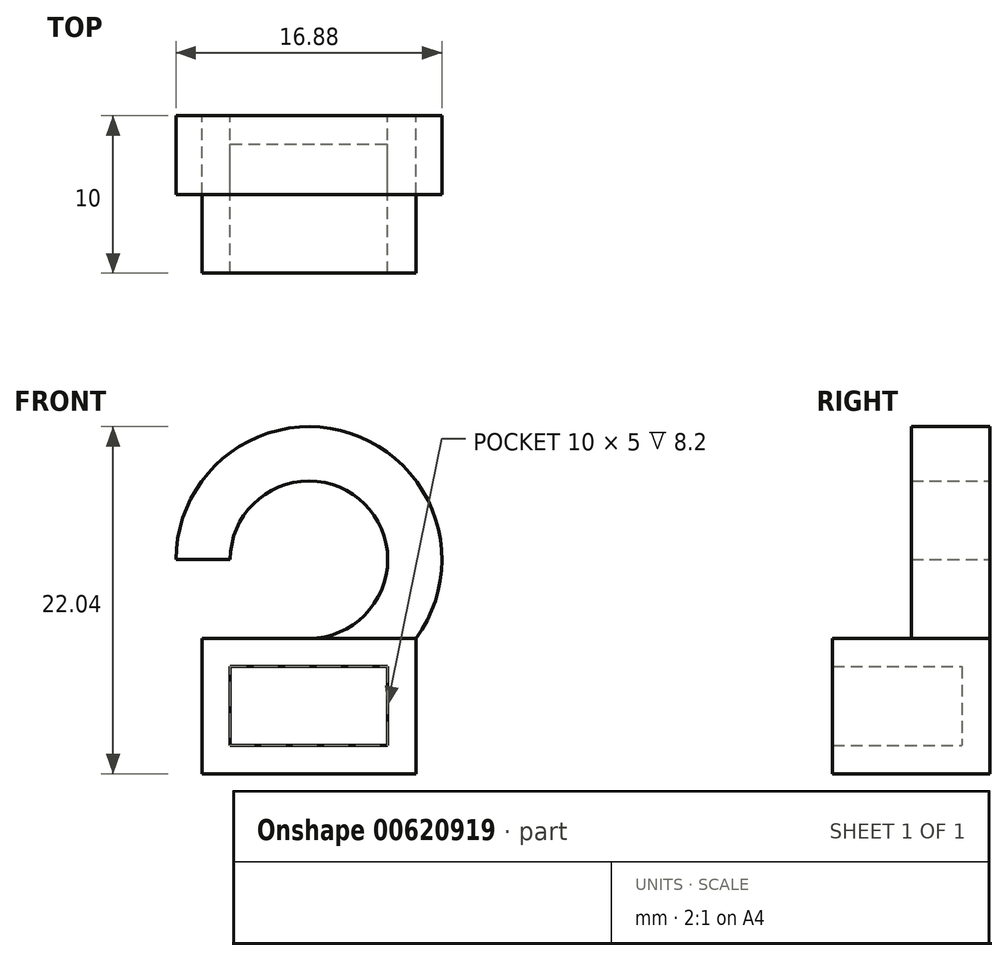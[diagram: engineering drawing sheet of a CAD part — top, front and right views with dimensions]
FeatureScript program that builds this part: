
annotation { "Feature Type Name" : "Feature", "Feature Type Description" : "" }
export const myFeature = defineFeature(function(context is Context, id is Id, definition is map)
    precondition{}
    {
        {
            var Q0;
            Q0=qCreatedBy(makeId("Front.planeOp"),FACE);
            var sketch = newSketch(context, id + "F0", { "sketchPlane" : qUnion([Q0])});
            skLineSegment(sketch, "E0.bottom", {"start": v(-5, 2.5) * mm, "end": v(5, 2.5) * mm});
            skLineSegment(sketch, "E0.top", {"start": v(-5, -2.5) * mm, "end": v(5, -2.5) * mm});
            skLineSegment(sketch, "E0.left", {"start": v(-5, 2.5) * mm, "end": v(-5, -2.5) * mm});
            skLineSegment(sketch, "E0.right", {"start": v(5, 2.5) * mm, "end": v(5, -2.5) * mm});
            skPoint(sketch, "E0.middle", {"position": v(0, 0) * mm});
            skLineSegment(sketch, "E1.bottom", {"start": v(-6.8, 4.3) * mm, "end": v(6.8, 4.3) * mm});
            skLineSegment(sketch, "E1.top", {"start": v(-6.8, -4.3) * mm, "end": v(6.8, -4.3) * mm});
            skLineSegment(sketch, "E1.left", {"start": v(-6.8, 4.3) * mm, "end": v(-6.8, -4.3) * mm});
            skLineSegment(sketch, "E1.right", {"start": v(6.8, 4.3) * mm, "end": v(6.8, -4.3) * mm});
            skLineSegment(sketch, "E2", {"start": v(0, 4.3) * mm, "end": v(0, 9.3) * mm});
            skPoint(sketch, "E2.endSnap0", {"position": v(0, 4.3) * mm});
            skArc(sketch, "E3", {"start": v(0, 4.3) * mm, "mid": v(3.54, 12.84) * mm, "end": v(-5, 9.3) * mm});
            skArc(sketch, "E4", {"start": v(-6.8, 4.3) * mm, "mid": v(8.02, 11.93) * mm, "end": v(-8.44, 9.3) * mm});
            skLineSegment(sketch, "E5", {"start": v(0, 9.3) * mm, "end": v(-8.44, 9.3) * mm});
            skSolve(sketch);
        }
        {
            var Q0;
            Q0=makeQuery(id+"F0.imprint","IMPRINT",FACE,{"disambiguationData":[TD([[makeQuery(id+"F0.imprint","IMPRINT",EDGE,{"derivedFrom":sQuery(id+"F0.wireOp",EDGE,"E0.top")}),-1.0]])]});
            var Q1;
            {var subQ1=sQuery(id+"F0.wireOp",EDGE,"E0.bottom");Q1=makeQuery(id+"F0.imprint","IMPRINT",FACE,{"disambiguationData":[TD([[makeQuery(id+"F0.imprint","IMPRINT",EDGE,{"derivedFrom":subQ1}),1.0]])]});}
            extrude(context, id + "F1", {"entities" : qUnion([Q0, Q1]), "depth" : 10 * mm, "offsetDistance" : 25 * mm});
        }
        {
            var Q0;
            {var subQ0=sQuery(id+"F0.wireOp",EDGE,"E0.bottom");Q0=makeQuery(id+"F0.imprint","IMPRINT",FACE,{"disambiguationData":[TD([[makeQuery(id+"F0.imprint","IMPRINT",EDGE,{"derivedFrom":subQ0}),-1.0]])]});}
            var Q1;
            Q1=makeQuery(id+"F0.imprint","IMPRINT",FACE,{"disambiguationData":[TD([[makeQuery(id+"F0.imprint","IMPRINT",EDGE,{"derivedFrom":sQuery(id+"F0.wireOp",EDGE,"E0.top")}),1.0]])]});
            extrude(context, id + "F2", {"entities" : qUnion([Q0, Q1]), "operationType" : NewBodyOperationType.ADD, "depth" : 1.8 * mm, "offsetDistance" : 25 * mm});
        }
        {
            var Q0;
            {var subQ3=sQuery(id+"F0.wireOp",EDGE,"E3");Q0=makeQuery(id+"F0.imprint","IMPRINT",FACE,{"disambiguationData":[TD([[makeQuery(id+"F0.imprint","IMPRINT",EDGE,{"derivedFrom":subQ3}),-1.0]])]});}
            extrude(context, id + "F3", {"entities" : qUnion([Q0]), "operationType" : NewBodyOperationType.ADD, "depth" : 5 * mm, "offsetDistance" : 25 * mm});
        }
    });
